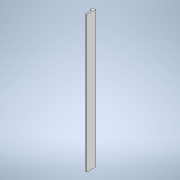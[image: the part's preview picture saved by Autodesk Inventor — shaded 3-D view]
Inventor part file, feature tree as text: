
AUTODESK INVENTOR PART (.ipt)
format: ipt  version: 2022 (Build 260153000, 153)  size: 98,816 bytes
history: native  units: mm
features: sketch x2, extrude x1
ambient origin geometry x8: Origin, YZ Plane, XZ Plane, XY Plane, X Axis, Y Axis, Z Axis, Center Point
bodies: Solid1 (feature_tree)
feature tree (3):
  sketch  "Sketch1"  dims[d0=44.0mm d1=10.0mm]
  extrude  "Extrusion1"  Depth=10.0mm
  sketch  "Sketch2"  dims[d2=10.0mm d3=65.0mm d4=1000.0mm d5=0.0mm]
